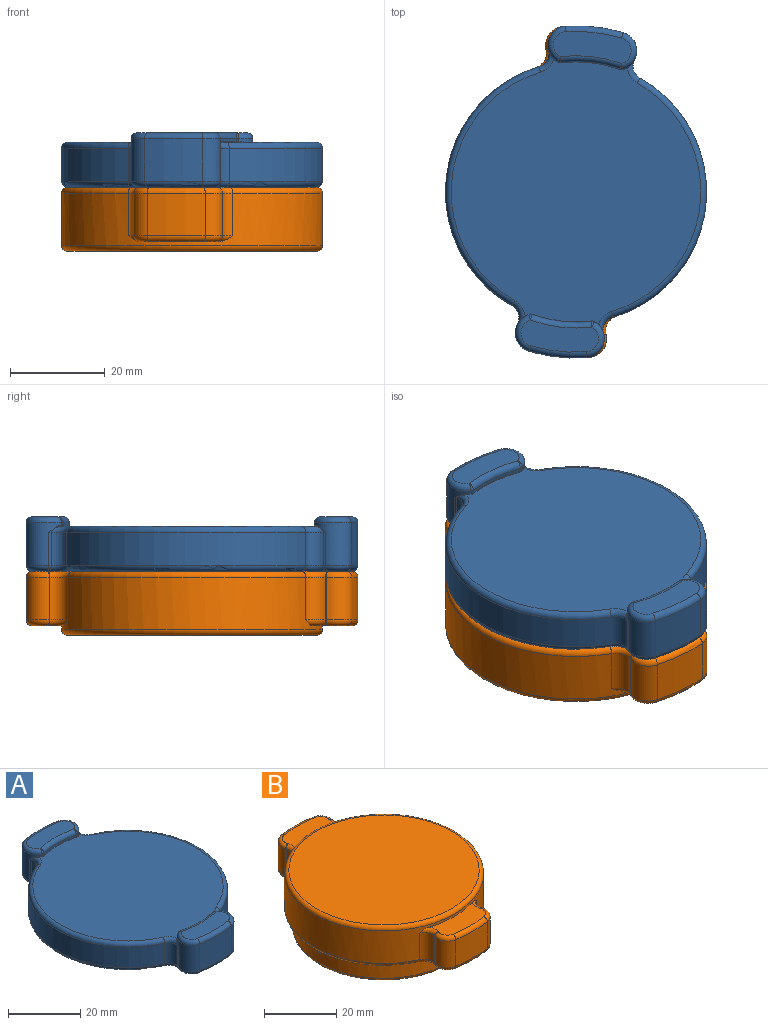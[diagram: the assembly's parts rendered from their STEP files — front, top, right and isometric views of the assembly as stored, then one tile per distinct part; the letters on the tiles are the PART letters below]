
ASSEMBLY  parts=2 mates=1
PART A: 143 faces, bbox 59.5x71.1x11.4 mm
  f0: cylinder r=25.5mm len=51mm, axis (0,0,1), area 979.1mm2, adj f2,f4,f6,f7,f126,f127,f128,f129
  f1: plane 48.69x24.08mm, normal (0,0,-1), area 96.1mm2, adj f2,f4,f88,f90,f95,f96,f97,f102
  f2: torus R=25.7mm, axis (0,0,1), area 6.4mm2, adj f0,f1,f137,f140
  f3: plane 34.3x24.08mm, normal (0,0,-1), area 83.7mm2, adj f7,f86,f87,f93,f95,f114,f120,f128
  f4: torus R=25.7mm, axis (0,0,1), area 6.4mm2, adj f0,f1,f133,f136
  f5: plane 14.62x14.62mm, normal (0,0,-1), area 12.4mm2, adj f6,f86,f88,f129,f132
  f6: torus R=25.7mm, axis (0,0,1), area 6.4mm2, adj f0,f5,f129,f132
  f7: torus R=25.7mm, axis (0,0,1), area 6.4mm2, adj f0,f3,f128,f141
  f8: cylinder r=27.5mm len=50.64mm, axis (0,0,1), area 450.5mm2, adj f41,f43,f46,f95
  f9: cylinder r=27.5mm len=50.64mm, axis (0,0,1), area 450.5mm2, adj f40,f42,f51,f88
  f10: plane 54.8x52.6mm, normal (0,0,1), area 2215.1mm2, adj f45,f46,f47,f50,f51,f52,f68,f69
  f11: plane 47.6x47.6mm, normal (0,0,-1), area 1779.5mm2, adj f124
  f12: cylinder r=24mm len=48mm, axis (0,0,1), area 90.5mm2, adj f124,f125
  f13: plane 50.6x50.6mm, normal (0,0,-1), area 171.1mm2, adj f125,f126
  f14: cylinder r=27.5mm len=12.62mm, axis (0,0,-1), area 8.9mm2, adj f36,f37,f63,f79
  f15: plane 7x0.46mm, normal (0.96,0.29,0), area 3.4mm2, adj f16,f41,f48,f99
  f16: cylinder r=4mm len=9mm, axis (0,0,-1), area 65.3mm2, adj f15,f17,f37,f60,f81,f82,f83,f98
  f17: cylinder r=35mm len=12.24mm, axis (0,0,-1), area 110.7mm2, adj f16,f18,f62,f96
  f18: cylinder r=4mm len=9mm, axis (0,0,-1), area 65.3mm2, adj f17,f19,f36,f64,f75,f76,f77,f94
  f19: plane 7x0.46mm, normal (-0.95,0.31,0), area 3.4mm2, adj f18,f40,f49,f92
  f20: plane 16.44x5.9mm, normal (0,0,1), area 79.6mm2, adj f60,f62,f63,f64
  f21: cylinder r=2.65mm len=9.8mm, axis (0,0,-1), area 163.2mm2, adj f100,f101,f102,f103,f104,f105
  f22: plane 4.9x4.9mm, normal (0,0,-1), area 18.9mm2, adj f105
  f23: cylinder r=2.65mm len=9.8mm, axis (0,0,-1), area 163.2mm2, adj f106,f107,f108,f109,f110,f111
  f24: plane 4.9x4.9mm, normal (0,0,-1), area 18.9mm2, adj f111
  f25: cylinder r=27.5mm len=12.62mm, axis (0,0,-1), area 8.9mm2, adj f38,f39,f58,f70
  f26: plane 7x0.46mm, normal (-0.96,-0.29,0), area 3.4mm2, adj f27,f42,f53,f84
  f27: cylinder r=4mm len=9mm, axis (0,0,-1), area 65.3mm2, adj f26,f28,f38,f57,f66,f67,f68,f85
  f28: cylinder r=35mm len=12.24mm, axis (0,0,-1), area 110.7mm2, adj f27,f29,f55,f87
  f29: cylinder r=4mm len=9mm, axis (0,0,-1), area 65.3mm2, adj f28,f30,f39,f54,f72,f73,f74,f89
  f30: plane 7x0.46mm, normal (0.95,-0.31,0), area 3.4mm2, adj f29,f43,f44,f91
  f31: plane 16.44x5.9mm, normal (0,0,1), area 79.6mm2, adj f54,f55,f57,f58
  f32: cylinder r=2.65mm len=9.8mm, axis (0,0,-1), area 163.2mm2, adj f112,f113,f114,f115,f116,f117
  f33: plane 4.9x4.9mm, normal (0,0,-1), area 18.9mm2, adj f117
  f34: cylinder r=2.65mm len=9.8mm, axis (0,0,-1), area 163.2mm2, adj f118,f119,f120,f121,f122,f123
  f35: plane 4.9x4.9mm, normal (0,0,-1), area 18.9mm2, adj f123
  f36: cylinder r=1mm len=0.7mm, axis (0,0,1), area 0.4mm2, adj f14,f18,f65,f78
  f37: cylinder r=1mm len=0.7mm, axis (0,0,1), area 0.4mm2, adj f14,f16,f61,f80
  f38: cylinder r=1mm len=0.7mm, axis (0,0,1), area 0.4mm2, adj f25,f27,f59,f69
  f39: cylinder r=1mm len=0.7mm, axis (0,0,1), area 0.4mm2, adj f25,f29,f56,f71
  f40: cylinder r=2.9mm len=7mm, axis (0,0,1), area 29.9mm2, adj f9,f19,f50,f90
  f41: cylinder r=2.9mm len=7mm, axis (0,0,1), area 29.9mm2, adj f8,f15,f47,f97
  f42: cylinder r=2.9mm len=7mm, axis (0,0,1), area 29.9mm2, adj f9,f26,f52,f86
  f43: cylinder r=2.9mm len=7mm, axis (0,0,1), area 29.9mm2, adj f8,f30,f45,f93
  f44: cylinder r=1.2mm len=0.46mm, axis (-0.31,-0.95,0), area 0.1mm2, adj f30,f45,f74
  f45: torus R=4.1mm, axis (0,0,1), area 7.5mm2, adj f10,f43,f44,f46,f73
  f46: torus R=26.3mm, axis (0,0,1), area 119.4mm2, adj f8,f10,f45,f47
  f47: torus R=4.1mm, axis (0,0,1), area 7.5mm2, adj f10,f41,f46,f48,f82
  f48: cylinder r=1.2mm len=0.47mm, axis (0.29,-0.96,0), area 0.1mm2, adj f15,f47,f83
  f49: cylinder r=1.2mm len=0.46mm, axis (0.31,0.95,0), area 0.1mm2, adj f19,f50,f75
  f50: torus R=4.1mm, axis (0,0,1), area 7.5mm2, adj f10,f40,f49,f51,f76
  f51: torus R=26.3mm, axis (0,0,1), area 119.4mm2, adj f9,f10,f50,f52
  f52: torus R=4.1mm, axis (0,0,1), area 7.5mm2, adj f10,f42,f51,f53,f67
  f53: cylinder r=1.2mm len=0.47mm, axis (-0.29,0.96,0), area 0.1mm2, adj f26,f52,f66
  f54: torus R=2.8mm, axis (0,0,-1), area 17.3mm2, adj f29,f31,f55,f56
  f55: torus R=33.8mm, axis (0,0,-1), area 22.9mm2, adj f28,f31,f54,f57
  f56: bspline ~1.27x1.26mm, area 0.5mm2, adj f39,f54,f58
  f57: torus R=2.8mm, axis (0,0,-1), area 17.3mm2, adj f27,f31,f55,f59
  f58: torus R=28.7mm, axis (0,0,-1), area 24.3mm2, adj f25,f31,f56,f59
  f59: bspline ~1.48x1.25mm, area 0.5mm2, adj f38,f57,f58
  f60: torus R=2.8mm, axis (0,0,-1), area 17.3mm2, adj f16,f20,f61,f62
  f61: bspline ~1.48x1.25mm, area 0.5mm2, adj f37,f60,f63
  f62: torus R=33.8mm, axis (0,0,-1), area 22.9mm2, adj f17,f20,f60,f64
  f63: torus R=28.7mm, axis (0,0,-1), area 24.3mm2, adj f14,f20,f61,f65
  f64: torus R=2.8mm, axis (0,0,-1), area 17.3mm2, adj f18,f20,f62,f65
  f65: bspline ~1.48x1.26mm, area 0.5mm2, adj f36,f63,f64
  f66: bspline ~0.64x0.39mm, area 0mm2, adj f27,f53,f67
  f67: bspline ~1.89x1.54mm, area 0.2mm2, adj f27,f52,f66,f68
  f68: torus R=4.1mm, axis (0,0,1), area 0.2mm2, adj f10,f27,f67,f69
  f69: torus R=1.1mm, axis (0,0,1), area 0.1mm2, adj f10,f38,f68,f70
  f70: torus R=27.4mm, axis (0,0,1), area 2mm2, adj f10,f25,f69,f71
  f71: torus R=1.1mm, axis (0,0,1), area 0.1mm2, adj f10,f39,f70,f72
  f72: torus R=4.1mm, axis (0,0,1), area 0.2mm2, adj f10,f29,f71,f73
  f73: bspline ~1.87x1.57mm, area 0.2mm2, adj f29,f45,f72,f74
  f74: bspline ~0.64x0.39mm, area 0mm2, adj f29,f44,f73
  f75: bspline ~0.64x0.39mm, area 0mm2, adj f18,f49,f76
  f76: bspline ~1.75x1.39mm, area 0.2mm2, adj f18,f50,f75,f77
  f77: torus R=4.1mm, axis (0,0,1), area 0.2mm2, adj f10,f18,f76,f78
  f78: torus R=1.1mm, axis (0,0,1), area 0.1mm2, adj f10,f36,f77,f79
  f79: torus R=27.4mm, axis (0,0,1), area 2mm2, adj f10,f14,f78,f80
  f80: torus R=1.1mm, axis (0,0,1), area 0.1mm2, adj f10,f37,f79,f81
  f81: torus R=4.1mm, axis (0,0,1), area 0.2mm2, adj f10,f16,f80,f82
  f82: bspline ~1.89x1.54mm, area 0.2mm2, adj f16,f47,f81,f83
  f83: bspline ~0.64x0.39mm, area 0mm2, adj f16,f48,f82
  f84: cylinder r=1.2mm len=1.28mm, axis (0.29,-0.96,0), area 0.9mm2, adj f26,f85,f86,f115
  f85: torus R=2.8mm, axis (0,0,1), area 11.1mm2, adj f27,f84,f87,f113
  f86: torus R=4.1mm, axis (0,0,1), area 9.3mm2, adj f3,f5,f42,f84,f88,f116
  f87: torus R=33.8mm, axis (0,0,1), area 22.9mm2, adj f3,f28,f85,f89,f112,f118
  f88: torus R=26.3mm, axis (0,0,1), area 119.4mm2, adj f1,f5,f9,f86,f90,f134
  f89: torus R=2.8mm, axis (0,0,1), area 11.1mm2, adj f29,f87,f91,f119
  f90: torus R=4.1mm, axis (0,0,1), area 9.3mm2, adj f1,f40,f88,f92,f110
  f91: cylinder r=1.2mm len=1.28mm, axis (0.31,0.95,0), area 0.9mm2, adj f30,f89,f93,f121
  f92: cylinder r=1.2mm len=1.28mm, axis (-0.31,-0.95,0), area 0.9mm2, adj f19,f90,f94,f109
  f93: torus R=4.1mm, axis (0,0,1), area 9.3mm2, adj f3,f43,f91,f95,f122
  f94: torus R=2.8mm, axis (0,0,1), area 11.1mm2, adj f18,f92,f96,f107
  f95: torus R=26.3mm, axis (0,0,1), area 119.4mm2, adj f1,f3,f8,f93,f97,f142
  f96: torus R=33.8mm, axis (0,0,1), area 22.9mm2, adj f1,f17,f94,f98,f100,f106
  f97: torus R=4.1mm, axis (0,0,1), area 9.3mm2, adj f1,f41,f95,f99,f104
  f98: torus R=2.8mm, axis (0,0,1), area 11.1mm2, adj f16,f96,f99,f101
  f99: cylinder r=1.2mm len=1.28mm, axis (-0.29,0.96,0), area 0.9mm2, adj f15,f97,f98,f103
  f100: bspline ~0.8x0.27mm, area 0.2mm2, adj f21,f96,f101,f102
  f101: torus R=2.85mm, axis (0,0,1), area 1.5mm2, adj f21,f98,f100,f103
  f102: torus R=2.85mm, axis (0,0,1), area 3.6mm2, adj f1,f21,f100,f104
  f103: bspline ~1.3x0.67mm, area 0.1mm2, adj f21,f99,f101,f104
  f104: bspline ~0.7x0.51mm, area 0mm2, adj f21,f97,f102,f103
  f105: torus R=2.45mm, axis (0,0,-1), area 5.1mm2, adj f21,f22
  f106: bspline ~1.48x0.42mm, area 0.2mm2, adj f23,f96,f107,f108
  f107: torus R=2.85mm, axis (0,0,-1), area 1.5mm2, adj f23,f94,f106,f109
  f108: torus R=2.85mm, axis (0,0,1), area 3.6mm2, adj f1,f23,f106,f110
  f109: bspline ~1.14x0.66mm, area 0.1mm2, adj f23,f92,f107,f110
  f110: bspline ~0.69x0.52mm, area 0mm2, adj f23,f90,f108,f109
  f111: torus R=2.45mm, axis (0,0,-1), area 5.1mm2, adj f23,f24
  f112: bspline ~0.8x0.27mm, area 0.2mm2, adj f32,f87,f113,f114
  f113: torus R=2.85mm, axis (0,0,1), area 1.5mm2, adj f32,f85,f112,f115
  f114: torus R=2.85mm, axis (0,0,1), area 3.6mm2, adj f3,f32,f112,f116
  f115: bspline ~1.3x0.67mm, area 0.1mm2, adj f32,f84,f113,f116
  f116: bspline ~0.7x0.51mm, area 0mm2, adj f32,f86,f114,f115
  f117: torus R=2.45mm, axis (0,0,-1), area 5.1mm2, adj f32,f33
  f118: bspline ~1.48x0.42mm, area 0.2mm2, adj f34,f87,f119,f120
  f119: torus R=2.85mm, axis (0,0,-1), area 1.5mm2, adj f34,f89,f118,f121
  f120: torus R=2.85mm, axis (0,0,1), area 3.6mm2, adj f3,f34,f118,f122
  f121: bspline ~1.14x0.66mm, area 0.1mm2, adj f34,f91,f119,f122
  f122: bspline ~0.69x0.52mm, area 0mm2, adj f34,f93,f120,f121
  f123: torus R=2.45mm, axis (0,0,-1), area 5.1mm2, adj f34,f35
  f124: torus R=23.8mm, axis (0,0,-1), area 47.2mm2, adj f11,f12
  f125: torus R=24.2mm, axis (0,0,1), area 47.5mm2, adj f12,f13
  f126: torus R=25.3mm, axis (0,0,1), area 50.2mm2, adj f0,f13
  f127: plane 19.9x2.7mm, normal (0,0,-1), area 16.1mm2, adj f0,f128,f129,f130
  f128: plane 2x0.74mm, normal (-0.93,0.38,0), area 1.6mm2, adj f0,f3,f7,f127,f130
  f129: plane 2x0.74mm, normal (0.93,0.38,0), area 1.6mm2, adj f0,f5,f6,f127,f130
  f130: cylinder r=26.3mm len=19.9mm, axis (0,0,-1), area 40.8mm2, adj f3,f127,f128,f129
  f131: plane 19.9x2.7mm, normal (0,0,-1), area 16.1mm2, adj f0,f132,f133,f134
  f132: plane 2x0.74mm, normal (-0.38,-0.93,0), area 1.6mm2, adj f0,f5,f6,f131,f134
  f133: plane 2x0.74mm, normal (-0.38,0.93,0), area 1.6mm2, adj f0,f1,f4,f131,f134
  f134: cylinder r=26.3mm len=19.9mm, axis (0,0,-1), area 40.8mm2, adj f88,f131,f132,f133
  f135: plane 19.9x2.7mm, normal (0,0,-1), area 16.1mm2, adj f0,f136,f137,f138
  f136: plane 2x0.74mm, normal (0.93,-0.38,0), area 1.6mm2, adj f0,f1,f4,f135,f138
  f137: plane 2x0.74mm, normal (-0.93,-0.38,0), area 1.6mm2, adj f0,f1,f2,f135,f138
  f138: cylinder r=26.3mm len=19.9mm, axis (0,0,-1), area 40.8mm2, adj f1,f135,f136,f137
  f139: plane 19.9x2.7mm, normal (0,0,-1), area 16.1mm2, adj f0,f140,f141,f142
  f140: plane 2x0.74mm, normal (0.38,0.93,0), area 1.6mm2, adj f0,f1,f2,f139,f142
  f141: plane 2x0.74mm, normal (0.38,-0.93,0), area 1.6mm2, adj f0,f3,f7,f139,f142
  f142: cylinder r=26.3mm len=19.9mm, axis (0,0,-1), area 40.8mm2, adj f95,f139,f140,f141
PART B: 163 faces, bbox 59.5x71.1x19.8 mm
  f0: plane 1.4x0.3mm, normal (-1,-0.03,0), area 0.4mm2, adj f12,f16,f18,f19
  f1: cylinder r=26mm len=1.2mm, axis (0,0,1), area 1.4mm2, adj f4,f8,f11,f12
  f2: plane 1.2x0.3mm, normal (1,-0.03,0), area 0.4mm2, adj f4,f6,f9,f10
  f3: plane 1.19x0.31mm, normal (0,0,-1), area 0.4mm2, adj f10,f11,f15,f16
  f4: cylinder r=0.2mm len=1.2mm, axis (0,0,1), area 0.4mm2, adj f1,f2,f5,f7
  f5: sphere r=0.2mm, area 0.1mm2, adj f4,f6,f8
  f6: cylinder r=0.2mm len=0.51mm, axis (-0.03,-1,0), area 0.1mm2, adj f2,f5,f9,f19
  f7: sphere r=0.2mm, area 0.1mm2, adj f4,f10,f11
  f8: torus R=25.8mm, axis (0,0,-1), area 0.4mm2, adj f1,f5,f12,f19
  f9: cylinder r=0.2mm len=1.4mm, axis (0,0,1), area 0.4mm2, adj f2,f6,f13,f20
  f10: cylinder r=0.2mm len=0.31mm, axis (0.03,1,0), area 0.1mm2, adj f2,f3,f7,f13
  f11: torus R=25.8mm, axis (0,0,-1), area 0.4mm2, adj f1,f3,f7,f14
  f12: cylinder r=0.2mm len=1.4mm, axis (0,0,1), area 0.4mm2, adj f0,f1,f8,f14,f19
  f13: sphere r=0.2mm, area 0.1mm2, adj f9,f10,f15
  f14: sphere r=0.2mm, area 0.1mm2, adj f11,f12,f16
  f15: torus R=25.5mm, axis (0,0,-1), area 0.4mm2, adj f3,f13,f17,f20
  f16: cylinder r=0.2mm len=0.31mm, axis (0.03,-1,0), area 0.1mm2, adj f0,f3,f14,f17
  f17: sphere r=0.2mm, area 0.1mm2, adj f15,f16,f18
  f18: cylinder r=0.2mm len=1.4mm, axis (0,0,1), area 0.4mm2, adj f0,f17,f19,f20
  f19: plane 67.6x52.6mm, normal (0,0,-1), area 304.2mm2, adj f0,f6,f8,f12,f18,f20,f64,f66
  f20: cylinder r=25.3mm len=50.6mm, axis (0,0,1), area 851.9mm2, adj f9,f15,f18,f19,f114,f120,f123,f133
  f21: plane 9x0.11mm, normal (0.96,0.29,0), area 1.1mm2, adj f22,f46,f54,f65
  f22: cylinder r=4mm len=9mm, axis (0,0,-1), area 61.2mm2, adj f21,f23,f53,f67
  f23: cylinder r=35mm len=12.24mm, axis (0,0,-1), area 110.7mm2, adj f22,f24,f52,f69
  f24: cylinder r=4mm len=9mm, axis (0,0,-1), area 61.2mm2, adj f23,f25,f51,f71
  f25: plane 9x0.11mm, normal (-0.95,0.31,0), area 1.1mm2, adj f24,f45,f50,f73
  f26: plane 16.64x7.65mm, normal (0,0,1), area 101mm2, adj f31,f49,f50,f51,f52,f53,f54,f55
  f27: cylinder r=2.65mm len=9.8mm, axis (0,0,-1), area 163.2mm2, adj f81,f82,f83,f84,f85,f86
  f28: plane 4.9x4.9mm, normal (0,0,-1), area 18.9mm2, adj f86
  f29: cylinder r=2.65mm len=9.8mm, axis (0,0,-1), area 163.2mm2, adj f87,f88,f89,f90,f91,f92
  f30: plane 4.9x4.9mm, normal (0,0,-1), area 18.9mm2, adj f92
  f31: cylinder r=27.5mm len=55mm, axis (0,0,1), area 1443mm2, adj f26,f37,f45,f46,f47,f48,f49,f55
  f32: plane 9x0.11mm, normal (-0.96,-0.29,0), area 1.1mm2, adj f33,f48,f61,f78
  f33: cylinder r=4mm len=9mm, axis (0,0,-1), area 61.2mm2, adj f32,f34,f60,f76
  f34: cylinder r=35mm len=12.24mm, axis (0,0,-1), area 110.7mm2, adj f33,f35,f59,f74
  f35: cylinder r=4mm len=9mm, axis (0,0,-1), area 61.2mm2, adj f34,f36,f58,f72
  f36: plane 9x0.11mm, normal (0.95,-0.31,0), area 1.1mm2, adj f35,f47,f57,f70
  f37: plane 16.64x7.65mm, normal (0,0,1), area 101mm2, adj f31,f56,f57,f58,f59,f60,f61,f62
  f38: cylinder r=2.65mm len=9.8mm, axis (0,0,-1), area 163.2mm2, adj f93,f94,f95,f96,f97,f98
  f39: plane 4.9x4.9mm, normal (0,0,-1), area 18.9mm2, adj f98
  f40: cylinder r=2.65mm len=9.8mm, axis (0,0,-1), area 163.2mm2, adj f99,f100,f101,f102,f103,f104
  f41: plane 4.9x4.9mm, normal (0,0,-1), area 18.9mm2, adj f104
  f42: plane 52.6x52.6mm, normal (0,0,1), area 2173mm2, adj f63
  f43: plane 44.2x44.2mm, normal (0,0,-1), area 1534.4mm2, adj f80
  f44: cylinder r=23.3mm len=46.6mm, axis (0,0,1), area 2196mm2, adj f80,f162
  f45: cylinder r=3.3mm len=9mm, axis (0,0,1), area 43.5mm2, adj f25,f31,f49,f75
  f46: cylinder r=3.3mm len=9mm, axis (0,0,1), area 43.5mm2, adj f21,f31,f55,f64
  f47: cylinder r=3.3mm len=9mm, axis (0,0,1), area 43.5mm2, adj f31,f36,f56,f68
  f48: cylinder r=3.3mm len=9mm, axis (0,0,1), area 43.5mm2, adj f31,f32,f62,f79
  f49: torus R=4.5mm, axis (0,0,-1), area 7.4mm2, adj f26,f31,f45,f50
  f50: cylinder r=1.2mm len=1.2mm, axis (-0.31,-0.95,0), area 0.2mm2, adj f25,f26,f49,f51
  f51: torus R=2.8mm, axis (0,0,-1), area 11.4mm2, adj f24,f26,f50,f52
  f52: torus R=33.8mm, axis (0,0,-1), area 22.9mm2, adj f23,f26,f51,f53
  f53: torus R=2.8mm, axis (0,0,-1), area 11.4mm2, adj f22,f26,f52,f54
  f54: cylinder r=1.2mm len=1.2mm, axis (-0.29,0.96,0), area 0.2mm2, adj f21,f26,f53,f55
  f55: torus R=4.5mm, axis (0,0,-1), area 7.4mm2, adj f26,f31,f46,f54
  f56: torus R=4.5mm, axis (0,0,-1), area 7.4mm2, adj f31,f37,f47,f57
  f57: cylinder r=1.2mm len=1.2mm, axis (0.31,0.95,0), area 0.2mm2, adj f36,f37,f56,f58
  f58: torus R=2.8mm, axis (0,0,-1), area 11.4mm2, adj f35,f37,f57,f59
  f59: torus R=33.8mm, axis (0,0,-1), area 22.9mm2, adj f34,f37,f58,f60
  f60: torus R=2.8mm, axis (0,0,-1), area 11.4mm2, adj f33,f37,f59,f61
  f61: cylinder r=1.2mm len=1.2mm, axis (0.29,-0.96,0), area 0.2mm2, adj f32,f37,f60,f62
  f62: torus R=4.5mm, axis (0,0,-1), area 7.4mm2, adj f31,f37,f48,f61
  f63: torus R=26.3mm, axis (0,0,1), area 320.5mm2, adj f31,f42
  f64: torus R=4.5mm, axis (0,0,-1), area 10.3mm2, adj f19,f46,f65,f66,f85
  f65: cylinder r=1.2mm len=1.2mm, axis (0.29,-0.96,0), area 0.2mm2, adj f21,f64,f67,f84
  f66: torus R=26.3mm, axis (0,0,-1), area 118.2mm2, adj f19,f31,f64,f68
  f67: torus R=2.8mm, axis (0,0,-1), area 11.1mm2, adj f22,f65,f69,f82
  f68: torus R=4.5mm, axis (0,0,-1), area 10.3mm2, adj f19,f47,f66,f70,f103
  f69: torus R=33.8mm, axis (0,0,-1), area 22.9mm2, adj f19,f23,f67,f71,f81,f87
  f70: cylinder r=1.2mm len=1.2mm, axis (-0.31,-0.95,0), area 0.2mm2, adj f36,f68,f72,f102
  f71: torus R=2.8mm, axis (0,0,-1), area 11.1mm2, adj f24,f69,f73,f88
  f72: torus R=2.8mm, axis (0,0,-1), area 11.1mm2, adj f35,f70,f74,f100
  f73: cylinder r=1.2mm len=1.2mm, axis (0.31,0.95,0), area 0.2mm2, adj f25,f71,f75,f90
  f74: torus R=33.8mm, axis (0,0,-1), area 22.9mm2, adj f19,f34,f72,f76,f93,f99
  f75: torus R=4.5mm, axis (0,0,-1), area 10.3mm2, adj f19,f45,f73,f77,f91
  f76: torus R=2.8mm, axis (0,0,-1), area 11.1mm2, adj f33,f74,f78,f94
  f77: torus R=26.3mm, axis (0,0,-1), area 118.2mm2, adj f19,f31,f75,f79
  f78: cylinder r=1.2mm len=1.2mm, axis (-0.29,0.96,0), area 0.2mm2, adj f32,f76,f79,f96
  f79: torus R=4.5mm, axis (0,0,-1), area 10.3mm2, adj f19,f48,f77,f78,f97
  f80: torus R=22.1mm, axis (0,0,1), area 270.8mm2, adj f43,f44
  f81: bspline ~0.8x0.27mm, area 0.2mm2, adj f27,f69,f82,f83
  f82: torus R=2.85mm, axis (0,0,1), area 1.5mm2, adj f27,f67,f81,f84
  f83: torus R=2.85mm, axis (0,0,-1), area 3.6mm2, adj f19,f27,f81,f85
  f84: bspline ~1.15x0.56mm, area 0mm2, adj f27,f65,f82,f85
  f85: bspline ~0.79x0.5mm, area 0.1mm2, adj f27,f64,f83,f84
  f86: torus R=2.45mm, axis (0,0,-1), area 5.1mm2, adj f27,f28
  f87: bspline ~1.48x0.42mm, area 0.2mm2, adj f29,f69,f88,f89
  f88: torus R=2.85mm, axis (0,0,-1), area 1.5mm2, adj f29,f71,f87,f90
  f89: torus R=2.85mm, axis (0,0,-1), area 3.6mm2, adj f19,f29,f87,f91
  f90: bspline ~0.86x0.52mm, area 0mm2, adj f29,f73,f88,f91
  f91: bspline ~0.79x0.51mm, area 0.1mm2, adj f29,f75,f89,f90
  f92: torus R=2.45mm, axis (0,0,-1), area 5.1mm2, adj f29,f30
  f93: bspline ~0.8x0.27mm, area 0.2mm2, adj f38,f74,f94,f95
  f94: torus R=2.85mm, axis (0,0,1), area 1.5mm2, adj f38,f76,f93,f96
  f95: torus R=2.85mm, axis (0,0,-1), area 3.6mm2, adj f19,f38,f93,f97
  f96: bspline ~1.15x0.56mm, area 0mm2, adj f38,f78,f94,f97
  f97: bspline ~0.79x0.5mm, area 0.1mm2, adj f38,f79,f95,f96
  f98: torus R=2.45mm, axis (0,0,-1), area 5.1mm2, adj f38,f39
  f99: bspline ~1.48x0.42mm, area 0.2mm2, adj f40,f74,f100,f101
  f100: torus R=2.85mm, axis (0,0,-1), area 1.5mm2, adj f40,f72,f99,f102
  f101: torus R=2.85mm, axis (0,0,-1), area 3.6mm2, adj f19,f40,f99,f103
  f102: bspline ~0.86x0.52mm, area 0mm2, adj f40,f70,f100,f103
  f103: bspline ~0.79x0.51mm, area 0.1mm2, adj f40,f68,f101,f102
  f104: torus R=2.45mm, axis (0,0,-1), area 5.1mm2, adj f40,f41
  f105: plane 1.4x0.3mm, normal (1,0.03,0), area 0.4mm2, adj f19,f117,f121,f123
  f106: cylinder r=26mm len=1.2mm, axis (0,0,1), area 1.4mm2, adj f109,f113,f116,f117
  f107: plane 1.2x0.3mm, normal (-1,0.03,0), area 0.4mm2, adj f109,f111,f114,f115
  f108: plane 1.19x0.31mm, normal (0,0,-1), area 0.4mm2, adj f115,f116,f120,f121
  f109: cylinder r=0.2mm len=1.2mm, axis (0,0,1), area 0.4mm2, adj f106,f107,f110,f112
  f110: sphere r=0.2mm, area 0.1mm2, adj f109,f111,f113
  f111: cylinder r=0.2mm len=0.51mm, axis (0.03,1,0), area 0.1mm2, adj f19,f107,f110,f114
  f112: sphere r=0.2mm, area 0.1mm2, adj f109,f115,f116
  f113: torus R=25.8mm, axis (0,0,-1), area 0.4mm2, adj f19,f106,f110,f117
  f114: cylinder r=0.2mm len=1.4mm, axis (0,0,1), area 0.4mm2, adj f20,f107,f111,f118
  f115: cylinder r=0.2mm len=0.31mm, axis (-0.03,-1,0), area 0.1mm2, adj f107,f108,f112,f118
  f116: torus R=25.8mm, axis (0,0,-1), area 0.4mm2, adj f106,f108,f112,f119
  f117: cylinder r=0.2mm len=1.4mm, axis (0,0,1), area 0.4mm2, adj f19,f105,f106,f113,f119
  f118: sphere r=0.2mm, area 0.1mm2, adj f114,f115,f120
  f119: sphere r=0.2mm, area 0.1mm2, adj f116,f117,f121
  f120: torus R=25.5mm, axis (0,0,-1), area 0.4mm2, adj f20,f108,f118,f122
  f121: cylinder r=0.2mm len=0.31mm, axis (-0.03,1,0), area 0.1mm2, adj f105,f108,f119,f122
  f122: sphere r=0.2mm, area 0.1mm2, adj f120,f121,f123
  f123: cylinder r=0.2mm len=1.4mm, axis (0,0,1), area 0.4mm2, adj f19,f20,f105,f122
  f124: plane 1.4x0.3mm, normal (-0.03,1,0), area 0.4mm2, adj f19,f136,f140,f142
  f125: cylinder r=26mm len=1.2mm, axis (0,0,1), area 1.4mm2, adj f128,f132,f135,f136
  f126: plane 1.2x0.3mm, normal (-0.03,-1,0), area 0.4mm2, adj f128,f130,f133,f134
  f127: plane 1.19x0.31mm, normal (0,0,-1), area 0.4mm2, adj f134,f135,f139,f140
  f128: cylinder r=0.2mm len=1.2mm, axis (0,0,1), area 0.4mm2, adj f125,f126,f129,f131
  f129: sphere r=0.2mm, area 0.1mm2, adj f128,f130,f132
  f130: cylinder r=0.2mm len=0.51mm, axis (-1,0.03,0), area 0.1mm2, adj f19,f126,f129,f133
  f131: sphere r=0.2mm, area 0.1mm2, adj f128,f134,f135
  f132: torus R=25.8mm, axis (0,0,-1), area 0.4mm2, adj f19,f125,f129,f136
  f133: cylinder r=0.2mm len=1.4mm, axis (0,0,1), area 0.4mm2, adj f20,f126,f130,f137
  f134: cylinder r=0.2mm len=0.31mm, axis (1,-0.03,0), area 0.1mm2, adj f126,f127,f131,f137
  f135: torus R=25.8mm, axis (0,0,-1), area 0.4mm2, adj f125,f127,f131,f138
  f136: cylinder r=0.2mm len=1.4mm, axis (0,0,1), area 0.4mm2, adj f19,f124,f125,f132,f138
  f137: sphere r=0.2mm, area 0.1mm2, adj f133,f134,f139
  f138: sphere r=0.2mm, area 0.1mm2, adj f135,f136,f140
  f139: torus R=25.5mm, axis (0,0,-1), area 0.4mm2, adj f20,f127,f137,f141
  f140: cylinder r=0.2mm len=0.31mm, axis (-1,-0.03,0), area 0.1mm2, adj f124,f127,f138,f141
  f141: sphere r=0.2mm, area 0.1mm2, adj f139,f140,f142
  f142: cylinder r=0.2mm len=1.4mm, axis (0,0,1), area 0.4mm2, adj f19,f20,f124,f141
  f143: plane 1.4x0.3mm, normal (0.03,-1,0), area 0.4mm2, adj f19,f155,f159,f161
  f144: cylinder r=26mm len=1.2mm, axis (0,0,1), area 1.4mm2, adj f147,f151,f154,f155
  f145: plane 1.2x0.3mm, normal (0.03,1,0), area 0.4mm2, adj f147,f149,f152,f153
  f146: plane 1.19x0.31mm, normal (0,0,-1), area 0.4mm2, adj f153,f154,f158,f159
  f147: cylinder r=0.2mm len=1.2mm, axis (0,0,1), area 0.4mm2, adj f144,f145,f148,f150
  f148: sphere r=0.2mm, area 0.1mm2, adj f147,f149,f151
  f149: cylinder r=0.2mm len=0.51mm, axis (1,-0.03,0), area 0.1mm2, adj f19,f145,f148,f152
  f150: sphere r=0.2mm, area 0.1mm2, adj f147,f153,f154
  f151: torus R=25.8mm, axis (0,0,-1), area 0.4mm2, adj f19,f144,f148,f155
  f152: cylinder r=0.2mm len=1.4mm, axis (0,0,1), area 0.4mm2, adj f20,f145,f149,f156
  f153: cylinder r=0.2mm len=0.31mm, axis (-1,0.03,0), area 0.1mm2, adj f145,f146,f150,f156
  f154: torus R=25.8mm, axis (0,0,-1), area 0.4mm2, adj f144,f146,f150,f157
  f155: cylinder r=0.2mm len=1.4mm, axis (0,0,1), area 0.4mm2, adj f19,f143,f144,f151,f157
  f156: sphere r=0.2mm, area 0.1mm2, adj f152,f153,f158
  f157: sphere r=0.2mm, area 0.1mm2, adj f154,f155,f159
  f158: torus R=25.5mm, axis (0,0,-1), area 0.4mm2, adj f20,f146,f156,f160
  f159: cylinder r=0.2mm len=0.31mm, axis (1,0.03,0), area 0.1mm2, adj f143,f146,f157,f160
  f160: sphere r=0.2mm, area 0.1mm2, adj f158,f159,f161
  f161: cylinder r=0.2mm len=1.4mm, axis (0,0,1), area 0.4mm2, adj f19,f20,f143,f160
  f162: torus R=24.3mm, axis (0,0,-1), area 479.7mm2, adj f20,f44
PLACE A rot(axis=(0,0,-1),6deg) t=(-17.13,-5.04,-4.35)mm
PLACE B rot(axis=(0.05,1,0),180deg) t=(-17.13,-5.04,-17.85)mm
MATE revolute A.f0 <-> B.f80  axis (0,0,1) through (-17.13,-5.04,-4.35)mm
